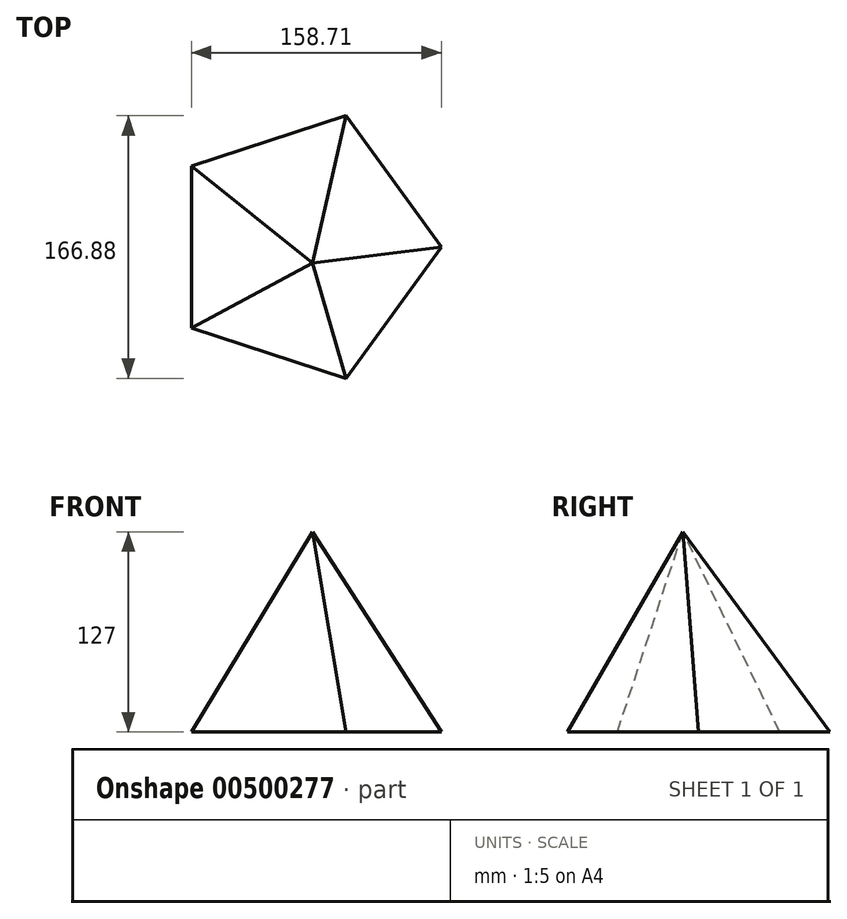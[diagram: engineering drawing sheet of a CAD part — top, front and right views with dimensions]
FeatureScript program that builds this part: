
annotation { "Feature Type Name" : "Feature", "Feature Type Description" : "" }
export const myFeature = defineFeature(function(context is Context, id is Id, definition is map)
    precondition{}
    {
        {
            var Q0;
            Q0=qCreatedBy(makeId("Top.planeOp"),FACE);
            var sketch = newSketch(context, id + "F0", { "sketchPlane" : qUnion([Q0])});
            skCircle(sketch, "E0.cCircle", {"center": v(0, 0) * mm, "radius": 87.73 * mm, "construction": true});
            skLineSegment(sketch, "E0.0", {"start": v(87.73, 0) * mm, "end": v(27.11, -83.44) * mm});
            skLineSegment(sketch, "E0.1", {"start": v(27.11, -83.44) * mm, "end": v(-70.98, -51.57) * mm});
            skLineSegment(sketch, "E0.2", {"start": v(-70.98, -51.57) * mm, "end": v(-70.98, 51.57) * mm});
            skLineSegment(sketch, "E0.3", {"start": v(-70.98, 51.57) * mm, "end": v(27.11, 83.44) * mm});
            skLineSegment(sketch, "E0.4", {"start": v(27.11, 83.44) * mm, "end": v(87.73, 0) * mm});
            skSolve(sketch);
        }
        {
            var Q0;
            Q0=qCreatedBy(makeId("Top.planeOp"),FACE);
            cPlane(context, id + "F1", {"entities" : qUnion([Q0]), "cplaneType" : CPlaneType.OFFSET, "offset" : 127 * mm, "width" : 152.4 * mm, "height" : 152.4 * mm});
        }
        {
            var Q0;
            Q0=qCreatedBy(id+"F1.planeOp",FACE);
            var sketch = newSketch(context, id + "F2", { "sketchPlane" : qUnion([Q0])});
            skPoint(sketch, "E1", {"position": v(5.97, -10.02) * mm});
            skSolve(sketch);
        }
        {
            var Q0;
            Q0=makeQuery(id+"F0.imprint","IMPRINT",FACE,{"disambiguationData":[TD([[makeQuery(id+"F0.imprint","IMPRINT",EDGE,{"derivedFrom":sQuery(id+"F0.wireOp",EDGE,"E0.0")}),-1.0]])]});
            var Q1;
            Q1=sQuery(id+"F2.wireOp",VERTEX,"E1");
            loft(context, id + "F3", {"sheetProfilesArray" : [{ "sheetProfileEntities" : qUnion([Q0]) }, { "sheetProfileEntities" : qUnion([Q1]) }]});
        }
    });
